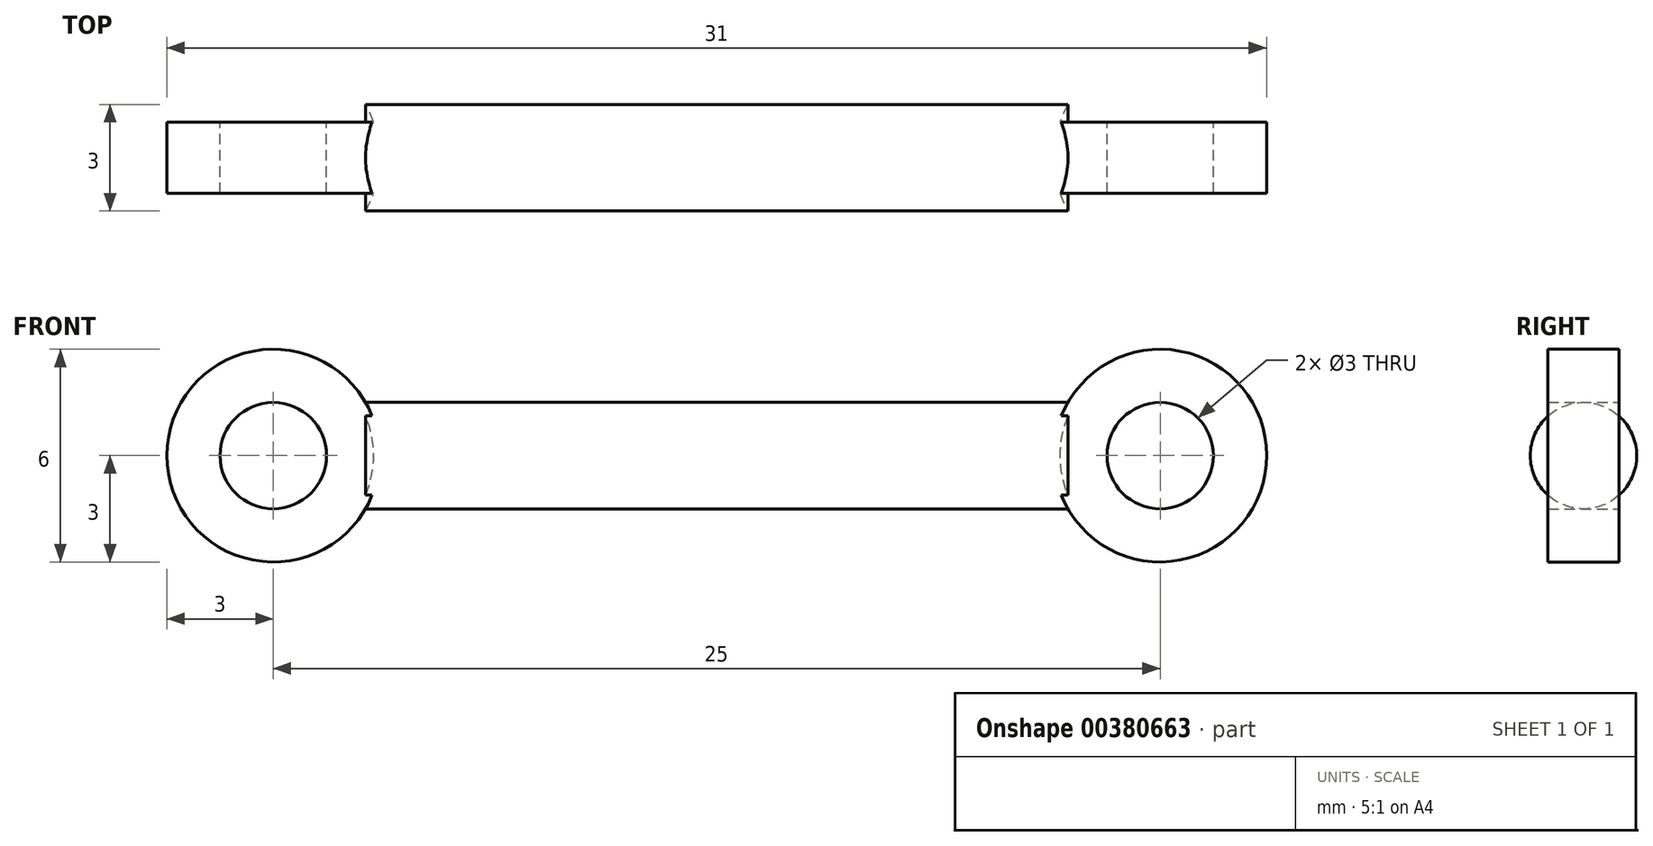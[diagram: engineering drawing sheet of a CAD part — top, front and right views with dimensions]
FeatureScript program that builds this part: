
annotation { "Feature Type Name" : "Feature", "Feature Type Description" : "" }
export const myFeature = defineFeature(function(context is Context, id is Id, definition is map)
    precondition{}
    {
        {
            var Q0;
            Q0=qCreatedBy(makeId("Front.planeOp"),FACE);
            var sketch = newSketch(context, id + "F0", { "sketchPlane" : qUnion([Q0])});
            skCircle(sketch, "E0", {"center": v(0, 0) * mm, "radius": 1.5 * mm});
            skArc(sketch, "E1", {"start": v(-2.6, -1.5) * mm, "mid": v(3, 0) * mm, "end": v(-2.6, 1.5) * mm});
            skCircle(sketch, "E2", {"center": v(-25, 0) * mm, "radius": 1.5 * mm});
            skArc(sketch, "E3", {"start": v(-22.4, 1.5) * mm, "mid": v(-28, 0) * mm, "end": v(-22.4, -1.5) * mm});
            skLineSegment(sketch, "E4", {"start": v(0, 1.5) * mm, "end": v(-25, 1.5) * mm});
            skLineSegment(sketch, "E5", {"start": v(-25, -1.5) * mm, "end": v(-22.4, -1.5) * mm});
            skCircle(sketch, "E6", {"center": v(-25, 0) * mm, "radius": 3 * mm});
            skCircle(sketch, "E7", {"center": v(0, 0) * mm, "radius": 3 * mm});
            skLineSegment(sketch, "E8.trimOffspring", {"start": v(-2.6, -1.5) * mm, "end": v(0, -1.5) * mm});
            skLineSegment(sketch, "E9", {"start": v(-22, 0) * mm, "end": v(-3, 0) * mm});
            skLineSegment(sketch, "E10", {"start": v(-24.05, 0) * mm, "end": v(6.6, 0) * mm, "construction": true});
            skPoint(sketch, "E10.startSnap0", {"position": v(-28, 0) * mm});
            skPoint(sketch, "E10.endSnap0", {"position": v(3, 0) * mm});
            skSolve(sketch);
        }
        {
            var Q0;
            {var subQ5=sQuery(id+"F0.wireOp",EDGE,"E9");Q0=makeQuery(id+"F0.imprint","IMPRINT",FACE,{"disambiguationData":[TD([[makeQuery(id+"F0.imprint","IMPRINT",EDGE,{"derivedFrom":subQ5}),1.0]])]});}
            var Q1;
            Q1=sQuery(id+"F0.wireOp",EDGE,"E10");
            revolve(context, id + "F1", {"entities" : qUnion([Q0]), "axis" : qUnion([Q1]), "revolveType" : RevolveType.FULL});
        }
        {
            var Q0;
            {var subQ3=sQuery(id+"F0.wireOp",EDGE,"E5");Q0=makeQuery(id+"F0.imprint","IMPRINT",FACE,{"disambiguationData":[TD([[makeQuery(id+"F0.imprint","IMPRINT",EDGE,{"derivedFrom":subQ3}),-1.0]])]});}
            var Q1;
            {var subQ3=sQuery(id+"F0.wireOp",EDGE,"E8.trimOffspring");Q1=makeQuery(id+"F0.imprint","IMPRINT",FACE,{"disambiguationData":[TD([[makeQuery(id+"F0.imprint","IMPRINT",EDGE,{"derivedFrom":subQ3}),-1.0]])]});}
            var Q2;
            {var subQ0=sQuery(id+"F0.wireOp",EDGE,"E8.trimOffspring");Q2=makeQuery(id+"F0.imprint","IMPRINT",FACE,{"disambiguationData":[TD([[makeQuery(id+"F0.imprint","IMPRINT",EDGE,{"derivedFrom":subQ0}),1.0]])]});}
            var Q3;
            {var subQ0=sQuery(id+"F0.wireOp",EDGE,"E5");Q3=makeQuery(id+"F0.imprint","IMPRINT",FACE,{"disambiguationData":[TD([[makeQuery(id+"F0.imprint","IMPRINT",EDGE,{"derivedFrom":subQ0}),1.0]])]});}
            extrude(context, id + "F2", {"entities" : qUnion([Q0, Q1, Q2, Q3]), "operationType" : NewBodyOperationType.ADD, "endBound" : BoundingType.SYMMETRIC, "depth" : 2 * mm});
        }
    });
